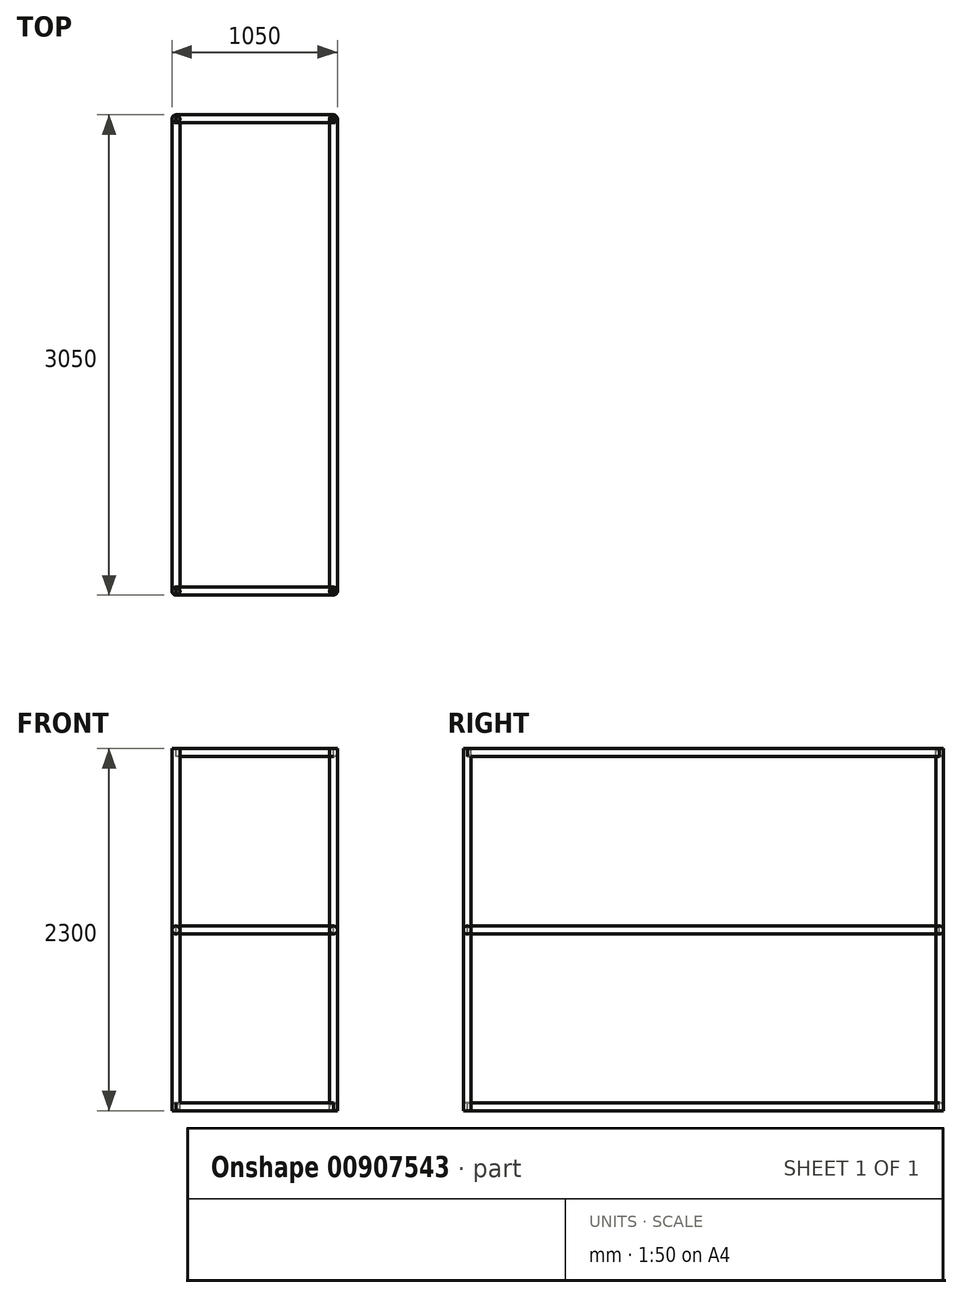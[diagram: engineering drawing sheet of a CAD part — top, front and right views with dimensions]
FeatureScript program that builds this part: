
annotation { "Feature Type Name" : "Feature", "Feature Type Description" : "" }
export const myFeature = defineFeature(function(context is Context, id is Id, definition is map)
    precondition{}
    {
        {
            var Q0;
            Q0=qCreatedBy(makeId("Right.planeOp"),FACE);
            var sketch = newSketch(context, id + "F0", { "sketchPlane" : qUnion([Q0])});
            skLineSegment(sketch, "E0.bottom", {"start": v(1500, -1152.5) * mm, "end": v(-1500, -1152.5) * mm});
            skLineSegment(sketch, "E0.top", {"start": v(1500, 1147.5) * mm, "end": v(-1500, 1147.5) * mm});
            skLineSegment(sketch, "E0.left", {"start": v(1500, -1152.5) * mm, "end": v(1500, 1147.5) * mm});
            skLineSegment(sketch, "E0.right", {"start": v(-1500, -1152.5) * mm, "end": v(-1500, 1147.5) * mm});
            skPoint(sketch, "E0.middle", {"position": v(0, -2.5) * mm});
            skPoint(sketch, "E1.middle", {"position": v(0, 0) * mm});
            skSolve(sketch);
        }
        {
            var Q0;
            Q0=qCreatedBy(makeId("Top.planeOp"),FACE);
            var sketch = newSketch(context, id + "F1", { "sketchPlane" : qUnion([Q0])});
            skLineSegment(sketch, "E2.bottom", {"start": v(500, -1500) * mm, "end": v(-500, -1500) * mm, "construction": true});
            skLineSegment(sketch, "E2.top", {"start": v(500, 1500) * mm, "end": v(-500, 1500) * mm, "construction": true});
            skLineSegment(sketch, "E2.left", {"start": v(500, -1500) * mm, "end": v(500, 1500) * mm, "construction": true});
            skLineSegment(sketch, "E2.right", {"start": v(-500, -1500) * mm, "end": v(-500, 1500) * mm, "construction": true});
            skPoint(sketch, "E2.middle", {"position": v(0, 0) * mm});
            skCircle(sketch, "E3", {"center": v(-500, 1500) * mm, "radius": 25 * mm});
            skCircle(sketch, "E4", {"center": v(500, 1500) * mm, "radius": 25 * mm});
            skCircle(sketch, "E5", {"center": v(500, -1500) * mm, "radius": 25 * mm});
            skCircle(sketch, "E6", {"center": v(-500, -1500) * mm, "radius": 25 * mm});
            skSolve(sketch);
        }
        {
            var Q0;
            Q0=qSketchRegion(id+"F1",true);
            extrude(context, id + "F2", {"entities" : qUnion([Q0]), "oppositeDirection" : true, "depth" : 2300 * mm, "offsetDistance" : 25 * mm});
        }
        {
            var Q0;
            Q0=qCreatedBy(makeId("Front.planeOp"),FACE);
            var sketch = newSketch(context, id + "F3", { "sketchPlane" : qUnion([Q0])});
            skCircle(sketch, "E7", {"center": v(500, -2275) * mm, "radius": 25 * mm});
            skCircle(sketch, "E8", {"center": v(-500, -2275) * mm, "radius": 25 * mm});
            skCircle(sketch, "E9", {"center": v(500, -25) * mm, "radius": 25 * mm});
            skCircle(sketch, "E10", {"center": v(500, -1152.5) * mm, "radius": 25 * mm});
            skCircle(sketch, "E11", {"center": v(-500, -1152.5) * mm, "radius": 25 * mm});
            skSolve(sketch);
        }
        {
            var Q0;
            Q0=qSketchRegion(id+"F3",true);
            extrude(context, id + "F4", {"entities" : qUnion([Q0]), "depth" : 1500 * mm, "offsetDistance" : 25 * mm, "hasSecondDirection" : true, "secondDirectionOppositeDirection" : true, "secondDirectionDepth" : 1500 * mm});
        }
        {
            var Q0;
            Q0=makeQuery(id+"F0.imprint","IMPRINT",FACE,{"disambiguationData":[TD([[makeQuery(id+"F0.imprint","IMPRINT",EDGE,{"derivedFrom":sQuery(id+"F0.wireOp",EDGE,"E0.bottom")}),-1.0]])]});
            var sketch = newSketch(context, id + "F5", { "sketchPlane" : qUnion([Q0])});
            skCircle(sketch, "E12", {"center": v(-1500, -2275) * mm, "radius": 25 * mm});
            skCircle(sketch, "E13", {"center": v(1500, -2275) * mm, "radius": 25 * mm});
            skCircle(sketch, "E14", {"center": v(1500, -25) * mm, "radius": 25 * mm});
            skCircle(sketch, "E15", {"center": v(-1500, -25) * mm, "radius": 25 * mm});
            skSolve(sketch);
        }
        {
            var Q0;
            Q0=qSketchRegion(id+"F5",true);
            extrude(context, id + "F6", {"entities" : qUnion([Q0]), "depth" : 500 * mm, "offsetDistance" : 25 * mm, "hasSecondDirection" : true, "secondDirectionOppositeDirection" : true, "secondDirectionDepth" : 500 * mm});
        }
        {
            var Q0;
            Q0=makeQuery(id+"F0.imprint","IMPRINT",FACE,{"disambiguationData":[TD([[makeQuery(id+"F0.imprint","IMPRINT",EDGE,{"derivedFrom":sQuery(id+"F0.wireOp",EDGE,"E0.bottom")}),-1.0]])]});
            var sketch = newSketch(context, id + "F7", { "sketchPlane" : qUnion([Q0])});
            skCircle(sketch, "E16", {"center": v(-1500, -1152.5) * mm, "radius": 25 * mm});
            skCircle(sketch, "E17", {"center": v(1500, -1152.5) * mm, "radius": 25 * mm});
            skSolve(sketch);
        }
        {
            var Q0;
            Q0=qSketchRegion(id+"F7",true);
            extrude(context, id + "F8", {"entities" : qUnion([Q0]), "depth" : 500 * mm, "offsetDistance" : 25 * mm, "hasSecondDirection" : true, "secondDirectionOppositeDirection" : true, "secondDirectionDepth" : 500 * mm});
        }
    });
